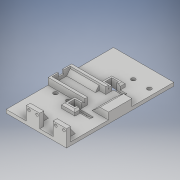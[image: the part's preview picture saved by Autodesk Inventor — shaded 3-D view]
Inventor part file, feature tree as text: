
AUTODESK INVENTOR PART (.ipt)
format: ipt  version: 2018 (Build 220112000, 112)  size: 476,160 bytes
history: native  units: in
note: dims shown in document units (in); Inventor stores cm internally (conversion verified against a paired STEP export)
features: extrude x27, sketch x27, chamfer x4, fillet x1
ambient origin geometry x8: Origin, YZ Plane, XZ Plane, XY Plane, X Axis, Y Axis, Z Axis, Center Point
bodies: Solid1 (feature_tree)
feature tree (59):
  extrude  "Extrusion1"  Depth=4.5in
  extrude  "Extrusion2"  Depth=1.75in
  chamfer  "Chamfer1"  Distance=0.4in
  extrude  "Extrusion3"  Depth=0.25in
  extrude  "Extrusion4"  Depth=0.25in
  fillet  "Fillet1"  Radius=0.25in
  extrude  "Extrusion5"  Depth=0.25in
  extrude  "Extrusion6"  Depth=0.125in TaperAngle=45.0deg
  extrude  "Extrusion7"  Depth=0.125in
  extrude  "Extrusion8"  Depth=0.25in
  extrude  "Extrusion9"  Depth=1.0in
  extrude  "Extrusion10"  Depth=0.25in
  extrude  "Extrusion11"  Depth=0.15in TaperAngle=0.0deg
  extrude  "Extrusion12"  Depth=1.75in
  extrude  "Extrusion13"  Depth=3.95in
  extrude  "Extrusion14"  Depth=1.35in
  extrude  "Extrusion15"  Depth=0.2in
  extrude  "Extrusion16"  Depth=0.35in
  extrude  "Extrusion17"  Depth=3.95in TaperAngle=0.0deg
  extrude  "Extrusion18"  Depth=0.5in TaperAngle=0.0deg
  extrude  "Extrusion21"  Depth=0.25in TaperAngle=0.0deg
  extrude  "Extrusion22"  Depth=0.2in TaperAngle=0.0deg
  extrude  "Extrusion23"  Depth=0.5in TaperAngle=0.0deg
  chamfer  "Chamfer2"  Distance=1.25in
  chamfer  "Chamfer3"  Distance=0.25in
  extrude  "Extrusion24"  Depth=0.35in
  extrude  "Extrusion25"  Depth=2.5in TaperAngle=0.0deg
  extrude  "Extrusion26"  Depth=0.3in
  chamfer  "Chamfer4"  Distance=0.3in
  extrude  "Extrusion27"  Depth=0.3in
  extrude  "Extrusion28"  Depth=0.3in
  extrude  "Extrusion29"  Depth=0.5in
  sketch  "Sketch1"  dims[d0=6.0in d1=4.5in]
  sketch  "Sketch2"  dims[d2=1.75in d3=1.75in]
  sketch  "Sketch3"  dims[d4=0.5in]
  sketch  "Sketch4"  dims[d5=0.5in]
  sketch  "Sketch5"  dims[d6=0.5in]
  sketch  "Sketch6"  dims[d7=0.5in]
  sketch  "Sketch7"  dims[d8=2.25in]
  sketch  "Sketch8"  dims[d9=1.375in d10=0.4in d11=0.0in]
  sketch  "Sketch9"  dims[d12=0.25in d13=0.25in]
  sketch  "Sketch10"  dims[d14=0.25in d15=0.25in d16=0.25in]
  sketch  "Sketch11"  dims[d17=0.25in d18=0.25in]
  sketch  "Sketch12"  dims[d19=0.35in d20=0.0in d21=0.125in d22=0.125in d23=45.0deg]
  sketch  "Sketch13"  dims[d24=0.25in d25=0.125in]
  sketch  "Sketch14"  dims[d26=0.125in d27=0.25in]
  sketch  "Sketch15"  dims[d28=0.35in d29=0.0in d30=1.0in]
  sketch  "Sketch16"  dims[d31=0.25in d32=0.25in]
  sketch  "Sketch17"  dims[d33=0.75in d34=0.15in d35=0.0in]
  sketch  "Sketch18"  dims[d36=0.84in d37=1.75in]
  sketch  "Sketch21"  dims[d38=0.0in d39=3.95in]
  sketch  "Sketch22"  dims[d40=0.5in d41=0.0in d42=1.35in]
  sketch  "Sketch23"  dims[d43=0.2in d44=0.82in]
  sketch  "Sketch24"  dims[d45=0.35in d46=0.35in]
  sketch  "Sketch25"  dims[d47=0.265in d48=3.95in d49=0.0in]
  sketch  "Sketch26"  dims[d50=0.15in d51=0.5in d52=0.0in]
  sketch  "Sketch27"  dims[d53=0.5in d54=0.0in d55=0.25in d56=0.0in]
  sketch  "Sketch28"  dims[d57=0.3in d58=0.0in d59=0.2in d60=0.0in]
  sketch  "Sketch29"  dims[d61=2.25in d62=0.5in d63=0.0in d64=1.25in d65=0.0in d66=0.25in d67=0.35in d68=2.5in d69=0.0in d70=0.3in d71=0.3in d72=0.3in d73=0.3in d74=0.8in d75=1.75in d76=0.25in d77=0.8in d78=1.75in d79=0.25in d80=0.25in d81=0.25in d82=0.4in d83=0.0in d84=1.0in d85=0.0in d86=1.0in d87=0.0in d88=0.0in d89=4.5in d90=0.15in d91=0.0in d96=2.0in d97=2.0in d98=0.3in d99=0.3in d100=0.5in d101=1.7in d102=0.055in d103=0.0in d104=1.0in d105=1.0in d106=1.0in d107=0.3in d108=1.0in d109=0.0in d110=0.3in d111=0.35in d112=0.35in d113=0.3in d114=0.7in d115=0.7in d116=1.0in d117=0.0in d118=0.7in d119=1.0in d120=45.0deg d121=0.7in d122=1.0in d123=45.0deg d124=0.2in d125=0.2in d126=0.2in d127=0.2in d128=0.2in d129=0.2in d130=0.2in d131=0.2in d132=0.2in d133=0.2in d134=0.2in d135=0.2in d136=1.0in d137=0.0in d138=0.121in d139=0.0in d140=0.0in d141=0.6in d142=0.51in d143=0.0in d144=0.6in d145=0.51in d146=45.0deg d147=0.01in d148=0.0in d149=0.1in d150=0.5in d151=0.0in d152=0.23in d153=0.21in d154=0.21in d155=0.0in d156=0.5in d157=0.0in]
